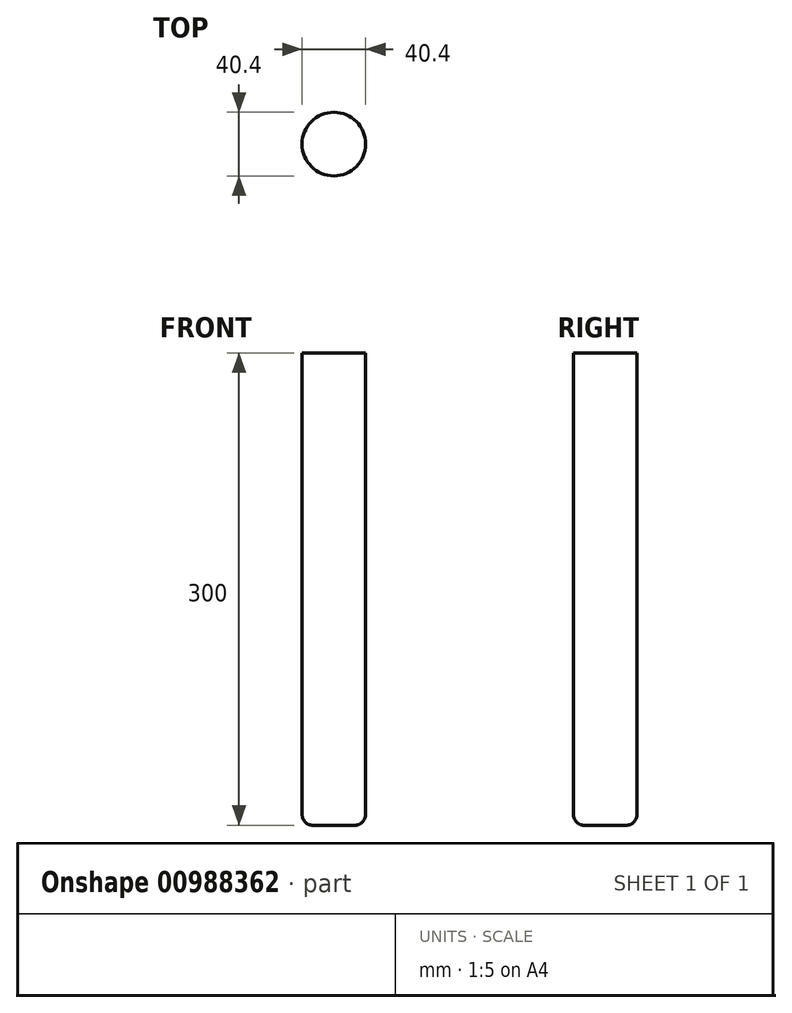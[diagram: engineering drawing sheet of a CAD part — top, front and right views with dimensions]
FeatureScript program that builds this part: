
annotation { "Feature Type Name" : "Feature", "Feature Type Description" : "" }
export const myFeature = defineFeature(function(context is Context, id is Id, definition is map)
    precondition{}
    {
        {
            var Q0;
            Q0=qCreatedBy(makeId("Top.planeOp"),FACE);
            var sketch = newSketch(context, id + "F0", { "sketchPlane" : qUnion([Q0])});
            skCircle(sketch, "E0", {"center": v(0, 0) * mm, "radius": 20.2 * mm});
            skSolve(sketch);
        }
        {
            var Q0;
            Q0=makeQuery(id+"F0.imprint","IMPRINT",FACE,{"disambiguationData":[TD([[makeQuery(id+"F0.imprint","IMPRINT",EDGE,{"derivedFrom":sQuery(id+"F0.wireOp",EDGE,"E0")}),1.0]])]});
            extrude(context, id + "F1", {"entities" : qUnion([Q0]), "depth" : 300 * mm, "offsetDistance" : 25 * mm});
        }
        {
            var Q0;
            Q0=makeQuery(id+"F1.opExtrude","CAP_EDGE",EDGE,{"disambiguationData":[OSD([sQuery(id+"F0.wireOp",EDGE,"E0")])],"isStart":true});
            fillet(context, id + "F2", {"entities" : qUnion([Q0]), "tangentPropagation" : true, "radius" : 7 * mm, "defaultsChanged" : true, "vertexSettings" : [], "allowEdgeOverflow" : false});
        }
    });
